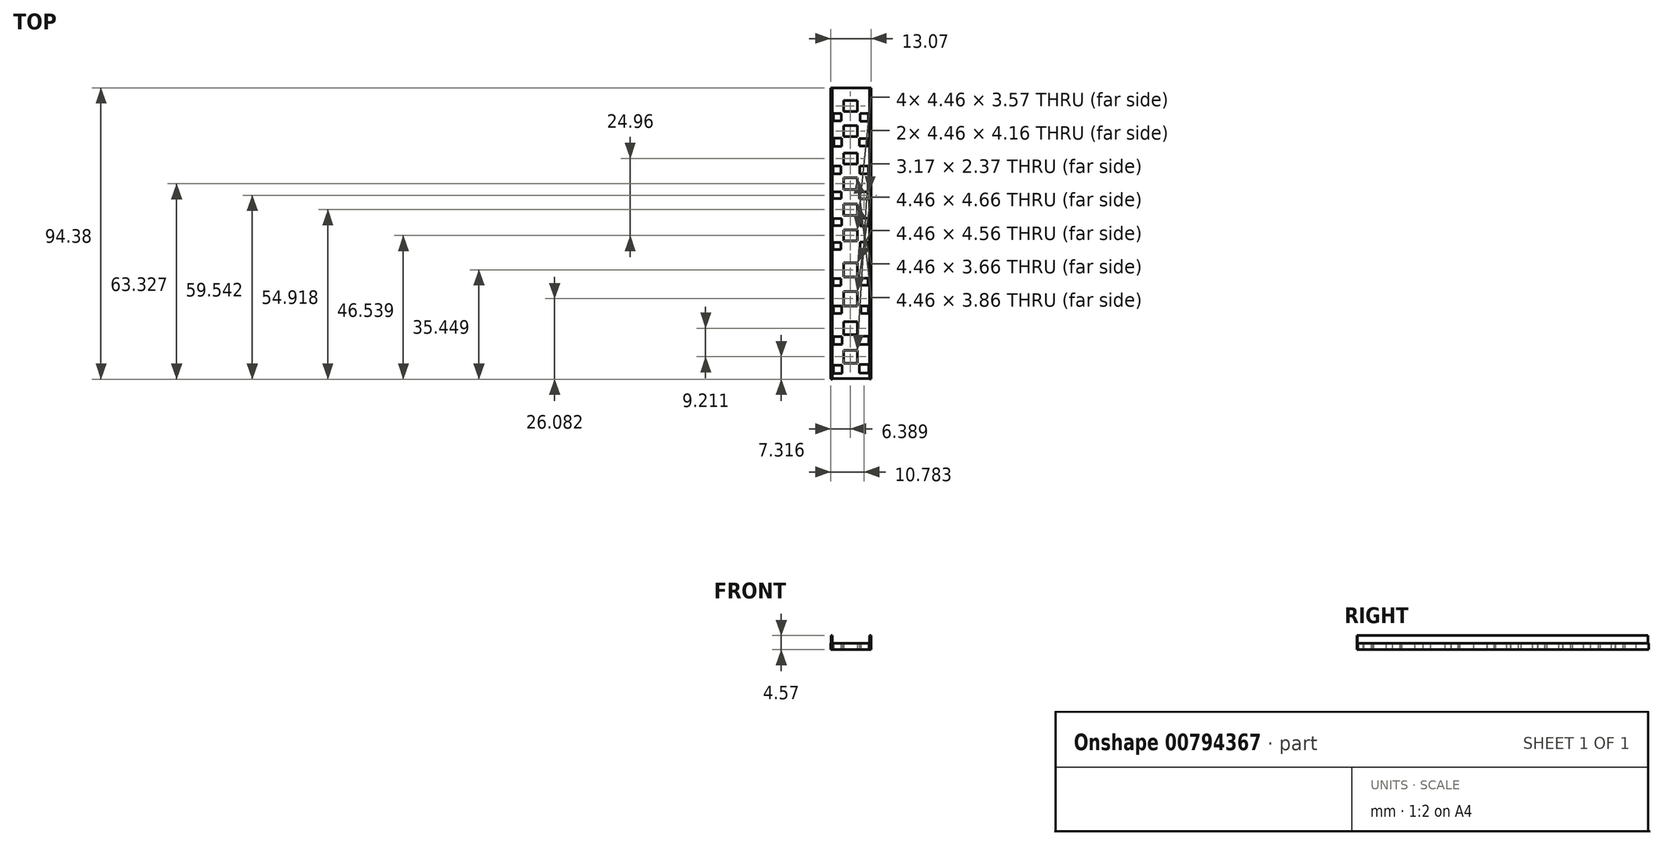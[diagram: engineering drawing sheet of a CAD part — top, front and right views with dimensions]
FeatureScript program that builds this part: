
annotation { "Feature Type Name" : "Feature", "Feature Type Description" : "" }
export const myFeature = defineFeature(function(context is Context, id is Id, definition is map)
    precondition{}
    {
        {
            var Q0;
            Q0=qCreatedBy(makeId("Top.planeOp"),FACE);
            var sketch = newSketch(context, id + "F0", { "sketchPlane" : qUnion([Q0])});
            skLineSegment(sketch, "E0", {"start": v(-36.42, 56.65) * mm, "end": v(-36.42, -37.55) * mm});
            skLineSegment(sketch, "E1", {"start": v(-36.42, -37.55) * mm, "end": v(-23.35, -37.55) * mm});
            skLineSegment(sketch, "E2", {"start": v(-23.35, -37.55) * mm, "end": v(-23.35, 56.65) * mm});
            skLineSegment(sketch, "E3", {"start": v(-23.35, 56.65) * mm, "end": v(-36.42, 56.65) * mm});
            skLineSegment(sketch, "E4.bottom", {"start": v(-32.26, 52.49) * mm, "end": v(-27.8, 52.49) * mm});
            skLineSegment(sketch, "E4.top", {"start": v(-32.26, 48.92) * mm, "end": v(-27.8, 48.92) * mm});
            skLineSegment(sketch, "E4.left", {"start": v(-32.26, 52.49) * mm, "end": v(-32.26, 48.92) * mm});
            skLineSegment(sketch, "E4.right", {"start": v(-27.8, 52.49) * mm, "end": v(-27.8, 48.92) * mm});
            skLineSegment(sketch, "E5.bottom", {"start": v(-32.26, 44.47) * mm, "end": v(-27.8, 44.47) * mm});
            skLineSegment(sketch, "E5.top", {"start": v(-32.26, 40.9) * mm, "end": v(-27.8, 40.9) * mm});
            skLineSegment(sketch, "E5.left", {"start": v(-32.26, 44.47) * mm, "end": v(-32.26, 40.9) * mm});
            skLineSegment(sketch, "E5.right", {"start": v(-27.8, 44.47) * mm, "end": v(-27.8, 40.9) * mm});
            skLineSegment(sketch, "E6.bottom", {"start": v(-32.26, 35.55) * mm, "end": v(-27.8, 35.55) * mm});
            skLineSegment(sketch, "E6.top", {"start": v(-32.26, 31.99) * mm, "end": v(-27.8, 31.99) * mm});
            skLineSegment(sketch, "E6.left", {"start": v(-32.26, 35.55) * mm, "end": v(-32.26, 31.99) * mm});
            skLineSegment(sketch, "E6.right", {"start": v(-27.8, 35.55) * mm, "end": v(-27.8, 31.99) * mm});
            skLineSegment(sketch, "E7.bottom", {"start": v(-32.26, 27.53) * mm, "end": v(-27.8, 27.53) * mm});
            skLineSegment(sketch, "E7.top", {"start": v(-32.26, 23.67) * mm, "end": v(-27.8, 23.67) * mm});
            skLineSegment(sketch, "E7.left", {"start": v(-32.26, 27.53) * mm, "end": v(-32.26, 23.67) * mm});
            skLineSegment(sketch, "E7.right", {"start": v(-27.8, 27.53) * mm, "end": v(-27.8, 23.67) * mm});
            skLineSegment(sketch, "E8.bottom", {"start": v(-32.26, 19.02) * mm, "end": v(-27.8, 19.02) * mm});
            skLineSegment(sketch, "E8.top", {"start": v(-32.26, 15.36) * mm, "end": v(-27.8, 15.36) * mm});
            skLineSegment(sketch, "E8.left", {"start": v(-32.26, 19.02) * mm, "end": v(-32.26, 15.36) * mm});
            skLineSegment(sketch, "E8.right", {"start": v(-27.8, 19.02) * mm, "end": v(-27.8, 15.36) * mm});
            skLineSegment(sketch, "E9.bottom", {"start": v(-32.26, 10.6) * mm, "end": v(-27.8, 10.6) * mm});
            skLineSegment(sketch, "E9.top", {"start": v(-32.26, 7.03) * mm, "end": v(-27.8, 7.03) * mm});
            skLineSegment(sketch, "E9.left", {"start": v(-32.26, 10.6) * mm, "end": v(-32.26, 7.03) * mm});
            skLineSegment(sketch, "E9.right", {"start": v(-27.8, 10.6) * mm, "end": v(-27.8, 7.03) * mm});
            skLineSegment(sketch, "E10.bottom", {"start": v(-32.26, 0) * mm, "end": v(-27.8, 0) * mm});
            skLineSegment(sketch, "E10.top", {"start": v(-32.26, -4.56) * mm, "end": v(-27.8, -4.56) * mm});
            skLineSegment(sketch, "E10.left", {"start": v(-32.26, 0) * mm, "end": v(-32.26, -4.56) * mm});
            skLineSegment(sketch, "E10.right", {"start": v(-27.8, 0) * mm, "end": v(-27.8, -4.56) * mm});
            skLineSegment(sketch, "E11.bottom", {"start": v(-32.26, -9.32) * mm, "end": v(-27.8, -9.32) * mm});
            skLineSegment(sketch, "E11.top", {"start": v(-32.26, -13.98) * mm, "end": v(-27.8, -13.98) * mm});
            skLineSegment(sketch, "E11.left", {"start": v(-32.26, -9.32) * mm, "end": v(-32.26, -13.98) * mm});
            skLineSegment(sketch, "E11.right", {"start": v(-27.8, -9.32) * mm, "end": v(-27.8, -13.98) * mm});
            skLineSegment(sketch, "E12.bottom", {"start": v(-32.26, -19.12) * mm, "end": v(-27.8, -19.12) * mm});
            skLineSegment(sketch, "E12.top", {"start": v(-32.26, -23.28) * mm, "end": v(-27.8, -23.28) * mm});
            skLineSegment(sketch, "E12.left", {"start": v(-32.26, -19.12) * mm, "end": v(-32.26, -23.28) * mm});
            skLineSegment(sketch, "E12.right", {"start": v(-27.8, -19.12) * mm, "end": v(-27.8, -23.28) * mm});
            skLineSegment(sketch, "E13.bottom", {"start": v(-32.26, -28.33) * mm, "end": v(-27.8, -28.33) * mm});
            skLineSegment(sketch, "E13.top", {"start": v(-32.26, -32.5) * mm, "end": v(-27.8, -32.5) * mm});
            skLineSegment(sketch, "E13.left", {"start": v(-32.26, -28.33) * mm, "end": v(-32.26, -32.5) * mm});
            skLineSegment(sketch, "E13.right", {"start": v(-27.8, -28.33) * mm, "end": v(-27.8, -32.5) * mm});
            skLineSegment(sketch, "E14.bottom", {"start": v(-32.75, -33.23) * mm, "end": v(-35.52, -33.23) * mm});
            skLineSegment(sketch, "E14.top", {"start": v(-32.75, -35.86) * mm, "end": v(-35.52, -35.86) * mm});
            skLineSegment(sketch, "E14.left", {"start": v(-32.75, -33.23) * mm, "end": v(-32.75, -35.86) * mm});
            skLineSegment(sketch, "E14.right", {"start": v(-35.52, -33.23) * mm, "end": v(-35.52, -35.86) * mm});
            skLineSegment(sketch, "E15.bottom", {"start": v(-24.16, -32.87) * mm, "end": v(-27.16, -32.87) * mm});
            skLineSegment(sketch, "E15.top", {"start": v(-24.16, -35.69) * mm, "end": v(-27.16, -35.69) * mm});
            skLineSegment(sketch, "E15.left", {"start": v(-24.16, -32.87) * mm, "end": v(-24.16, -35.69) * mm});
            skLineSegment(sketch, "E15.right", {"start": v(-27.16, -32.87) * mm, "end": v(-27.16, -35.69) * mm});
            skLineSegment(sketch, "E16.bottom", {"start": v(-32.8, -23.95) * mm, "end": v(-35.6, -23.95) * mm});
            skLineSegment(sketch, "E16.top", {"start": v(-32.8, -26.4) * mm, "end": v(-35.6, -26.4) * mm});
            skLineSegment(sketch, "E16.left", {"start": v(-32.8, -23.95) * mm, "end": v(-32.8, -26.4) * mm});
            skLineSegment(sketch, "E16.right", {"start": v(-35.6, -23.95) * mm, "end": v(-35.6, -26.4) * mm});
            skLineSegment(sketch, "E17.bottom", {"start": v(-24.16, -23.77) * mm, "end": v(-27.16, -23.77) * mm});
            skLineSegment(sketch, "E17.top", {"start": v(-24.16, -26.4) * mm, "end": v(-27.16, -26.4) * mm});
            skLineSegment(sketch, "E17.left", {"start": v(-24.16, -23.77) * mm, "end": v(-24.16, -26.4) * mm});
            skLineSegment(sketch, "E17.right", {"start": v(-27.16, -23.77) * mm, "end": v(-27.16, -26.4) * mm});
            skLineSegment(sketch, "E18.bottom", {"start": v(-32.84, -14.04) * mm, "end": v(-35.6, -14.04) * mm});
            skLineSegment(sketch, "E18.top", {"start": v(-32.84, -16.4) * mm, "end": v(-35.6, -16.4) * mm});
            skLineSegment(sketch, "E18.left", {"start": v(-32.84, -14.04) * mm, "end": v(-32.84, -16.4) * mm});
            skLineSegment(sketch, "E18.right", {"start": v(-35.6, -14.04) * mm, "end": v(-35.6, -16.4) * mm});
            skLineSegment(sketch, "E19.bottom", {"start": v(-24.22, -13.98) * mm, "end": v(-26.7, -13.98) * mm});
            skLineSegment(sketch, "E19.top", {"start": v(-24.22, -16.45) * mm, "end": v(-26.7, -16.45) * mm});
            skLineSegment(sketch, "E19.left", {"start": v(-24.22, -13.98) * mm, "end": v(-24.22, -16.45) * mm});
            skLineSegment(sketch, "E19.right", {"start": v(-26.7, -13.98) * mm, "end": v(-26.7, -16.45) * mm});
            skLineSegment(sketch, "E20.bottom", {"start": v(-33.14, -5.11) * mm, "end": v(-35.65, -5.11) * mm});
            skLineSegment(sketch, "E20.top", {"start": v(-33.14, -7.37) * mm, "end": v(-35.65, -7.37) * mm});
            skLineSegment(sketch, "E20.left", {"start": v(-33.14, -5.11) * mm, "end": v(-33.14, -7.37) * mm});
            skLineSegment(sketch, "E20.right", {"start": v(-35.65, -5.11) * mm, "end": v(-35.65, -7.37) * mm});
            skLineSegment(sketch, "E21.bottom", {"start": v(-24.36, -4.97) * mm, "end": v(-26.94, -4.97) * mm});
            skLineSegment(sketch, "E21.top", {"start": v(-24.36, -7.27) * mm, "end": v(-26.94, -7.27) * mm});
            skLineSegment(sketch, "E21.left", {"start": v(-24.36, -4.97) * mm, "end": v(-24.36, -7.27) * mm});
            skLineSegment(sketch, "E21.right", {"start": v(-26.94, -4.97) * mm, "end": v(-26.94, -7.27) * mm});
            skLineSegment(sketch, "E22.bottom", {"start": v(-33.1, 6.58) * mm, "end": v(-35.65, 6.58) * mm});
            skLineSegment(sketch, "E22.top", {"start": v(-33.1, 4.25) * mm, "end": v(-35.65, 4.25) * mm});
            skLineSegment(sketch, "E22.left", {"start": v(-33.1, 6.58) * mm, "end": v(-33.1, 4.25) * mm});
            skLineSegment(sketch, "E22.right", {"start": v(-35.65, 6.58) * mm, "end": v(-35.65, 4.25) * mm});
            skLineSegment(sketch, "E23.bottom", {"start": v(-24.07, 6.65) * mm, "end": v(-26.94, 6.65) * mm});
            skLineSegment(sketch, "E23.top", {"start": v(-24.07, 4.33) * mm, "end": v(-26.94, 4.33) * mm});
            skLineSegment(sketch, "E23.left", {"start": v(-24.07, 6.65) * mm, "end": v(-24.07, 4.33) * mm});
            skLineSegment(sketch, "E23.right", {"start": v(-26.94, 6.65) * mm, "end": v(-26.94, 4.33) * mm});
            skPoint(sketch, "E24.firstSnap0", {"position": v(-32.84, -15.22) * mm});
            skLineSegment(sketch, "E24.bottom", {"start": v(-32.84, 14.37) * mm, "end": v(-35.65, 14.37) * mm});
            skLineSegment(sketch, "E24.top", {"start": v(-32.84, 12.04) * mm, "end": v(-35.65, 12.04) * mm});
            skLineSegment(sketch, "E24.left", {"start": v(-32.84, 14.37) * mm, "end": v(-32.84, 12.04) * mm});
            skLineSegment(sketch, "E24.right", {"start": v(-35.65, 14.37) * mm, "end": v(-35.65, 12.04) * mm});
            skLineSegment(sketch, "E25.bottom", {"start": v(-24.03, 14.4) * mm, "end": v(-26.94, 14.4) * mm});
            skLineSegment(sketch, "E25.top", {"start": v(-24.03, 11.93) * mm, "end": v(-26.94, 11.93) * mm});
            skLineSegment(sketch, "E25.left", {"start": v(-24.03, 14.4) * mm, "end": v(-24.03, 11.93) * mm});
            skLineSegment(sketch, "E25.right", {"start": v(-26.94, 14.4) * mm, "end": v(-26.94, 11.93) * mm});
            skLineSegment(sketch, "E26.bottom", {"start": v(-33.07, 22.95) * mm, "end": v(-35.8, 22.95) * mm});
            skLineSegment(sketch, "E26.top", {"start": v(-33.07, 20.78) * mm, "end": v(-35.8, 20.78) * mm});
            skLineSegment(sketch, "E26.left", {"start": v(-33.07, 22.95) * mm, "end": v(-33.07, 20.78) * mm});
            skLineSegment(sketch, "E26.right", {"start": v(-35.8, 22.95) * mm, "end": v(-35.8, 20.78) * mm});
            skLineSegment(sketch, "E27.bottom", {"start": v(-24.05, 23) * mm, "end": v(-27.22, 23) * mm});
            skLineSegment(sketch, "E27.top", {"start": v(-24.05, 20.63) * mm, "end": v(-27.22, 20.63) * mm});
            skLineSegment(sketch, "E27.left", {"start": v(-24.05, 23) * mm, "end": v(-24.05, 20.63) * mm});
            skLineSegment(sketch, "E27.right", {"start": v(-27.22, 23) * mm, "end": v(-27.22, 20.63) * mm});
            skLineSegment(sketch, "E28.bottom", {"start": v(-33.12, 31.31) * mm, "end": v(-35.74, 31.31) * mm});
            skLineSegment(sketch, "E28.top", {"start": v(-33.12, 28.8) * mm, "end": v(-35.74, 28.8) * mm});
            skLineSegment(sketch, "E28.left", {"start": v(-33.12, 31.31) * mm, "end": v(-33.12, 28.8) * mm});
            skLineSegment(sketch, "E28.right", {"start": v(-35.74, 31.31) * mm, "end": v(-35.74, 28.8) * mm});
            skLineSegment(sketch, "E29.bottom", {"start": v(-27.02, 31.31) * mm, "end": v(-24.25, 31.31) * mm});
            skLineSegment(sketch, "E29.top", {"start": v(-27.02, 28.84) * mm, "end": v(-24.25, 28.84) * mm});
            skLineSegment(sketch, "E29.left", {"start": v(-27.02, 31.31) * mm, "end": v(-27.02, 28.84) * mm});
            skLineSegment(sketch, "E29.right", {"start": v(-24.25, 31.31) * mm, "end": v(-24.25, 28.84) * mm});
            skLineSegment(sketch, "E30.bottom", {"start": v(-32.84, 40.36) * mm, "end": v(-35.47, 40.36) * mm});
            skLineSegment(sketch, "E30.top", {"start": v(-32.84, 37.73) * mm, "end": v(-35.47, 37.73) * mm});
            skLineSegment(sketch, "E30.left", {"start": v(-32.84, 40.36) * mm, "end": v(-32.84, 37.73) * mm});
            skLineSegment(sketch, "E30.right", {"start": v(-35.47, 40.36) * mm, "end": v(-35.47, 37.73) * mm});
            skLineSegment(sketch, "E31.bottom", {"start": v(-24.25, 40.26) * mm, "end": v(-27.22, 40.26) * mm});
            skLineSegment(sketch, "E31.top", {"start": v(-24.25, 37.83) * mm, "end": v(-27.22, 37.83) * mm});
            skLineSegment(sketch, "E31.left", {"start": v(-24.25, 40.26) * mm, "end": v(-24.25, 37.83) * mm});
            skLineSegment(sketch, "E31.right", {"start": v(-27.22, 40.26) * mm, "end": v(-27.22, 37.83) * mm});
            skLineSegment(sketch, "E32.bottom", {"start": v(-32.98, 48.3) * mm, "end": v(-35.5, 48.3) * mm});
            skLineSegment(sketch, "E32.top", {"start": v(-32.98, 45.94) * mm, "end": v(-35.5, 45.94) * mm});
            skLineSegment(sketch, "E32.left", {"start": v(-32.98, 48.3) * mm, "end": v(-32.98, 45.94) * mm});
            skLineSegment(sketch, "E32.right", {"start": v(-35.5, 48.3) * mm, "end": v(-35.5, 45.94) * mm});
            skLineSegment(sketch, "E33.bottom", {"start": v(-26.86, 48.35) * mm, "end": v(-24.25, 48.35) * mm});
            skLineSegment(sketch, "E33.top", {"start": v(-26.86, 45.79) * mm, "end": v(-24.25, 45.79) * mm});
            skLineSegment(sketch, "E33.left", {"start": v(-26.86, 48.35) * mm, "end": v(-26.86, 45.79) * mm});
            skLineSegment(sketch, "E33.right", {"start": v(-24.25, 48.35) * mm, "end": v(-24.25, 45.79) * mm});
            skSolve(sketch);
        }
        {
            var Q0;
            Q0=makeQuery(id+"F0.imprint","IMPRINT",FACE,{"disambiguationData":[TD([[makeQuery(id+"F0.imprint","IMPRINT",EDGE,{"derivedFrom":sQuery(id+"F0.wireOp",EDGE,"E0")}),1.0]])]});
            extrude(context, id + "F1", {"entities" : qUnion([Q0]), "depth" : 2.03 * mm, "offsetDistance" : 25.4 * mm});
        }
        {
            var Q0;
            Q0=qCreatedBy(makeId("Top.planeOp"),FACE);
            var sketch = newSketch(context, id + "F2", { "sketchPlane" : qUnion([Q0])});
            skLineSegment(sketch, "E34.bottom", {"start": v(-36.35, -37.73) * mm, "end": v(-35.96, -37.73) * mm});
            skLineSegment(sketch, "E34.top", {"start": v(-36.35, 56.38) * mm, "end": v(-35.96, 56.38) * mm});
            skLineSegment(sketch, "E34.left", {"start": v(-36.35, -37.73) * mm, "end": v(-36.35, 56.38) * mm});
            skLineSegment(sketch, "E34.right", {"start": v(-35.96, -37.73) * mm, "end": v(-35.96, 56.38) * mm});
            skLineSegment(sketch, "E35.bottom", {"start": v(-41.68, 51.74) * mm, "end": v(-41.68, 51.74) * mm});
            skLineSegment(sketch, "E35.top", {"start": v(-41.68, 53.08) * mm, "end": v(-41.68, 53.08) * mm});
            skLineSegment(sketch, "E35.left", {"start": v(-41.68, 51.74) * mm, "end": v(-41.68, 53.08) * mm});
            skLineSegment(sketch, "E35.right", {"start": v(-41.68, 51.74) * mm, "end": v(-41.68, 53.08) * mm});
            skLineSegment(sketch, "E36.bottom", {"start": v(-23.43, -37.6) * mm, "end": v(-23.84, -37.6) * mm});
            skLineSegment(sketch, "E36.top", {"start": v(-23.43, 56.4) * mm, "end": v(-23.84, 56.4) * mm});
            skLineSegment(sketch, "E36.left", {"start": v(-23.43, -37.6) * mm, "end": v(-23.43, 56.4) * mm});
            skLineSegment(sketch, "E36.right", {"start": v(-23.84, -37.6) * mm, "end": v(-23.84, 56.4) * mm});
            skSolve(sketch);
        }
        {
            var Q0;
            Q0 = qSketchRegion(id + "F2", true);
            extrude(context, id + "F3", {"entities" : qUnion([Q0]), "operationType" : NewBodyOperationType.ADD, "depth" : 4.57 * mm, "offsetDistance" : 25.4 * mm});
        }
    });
